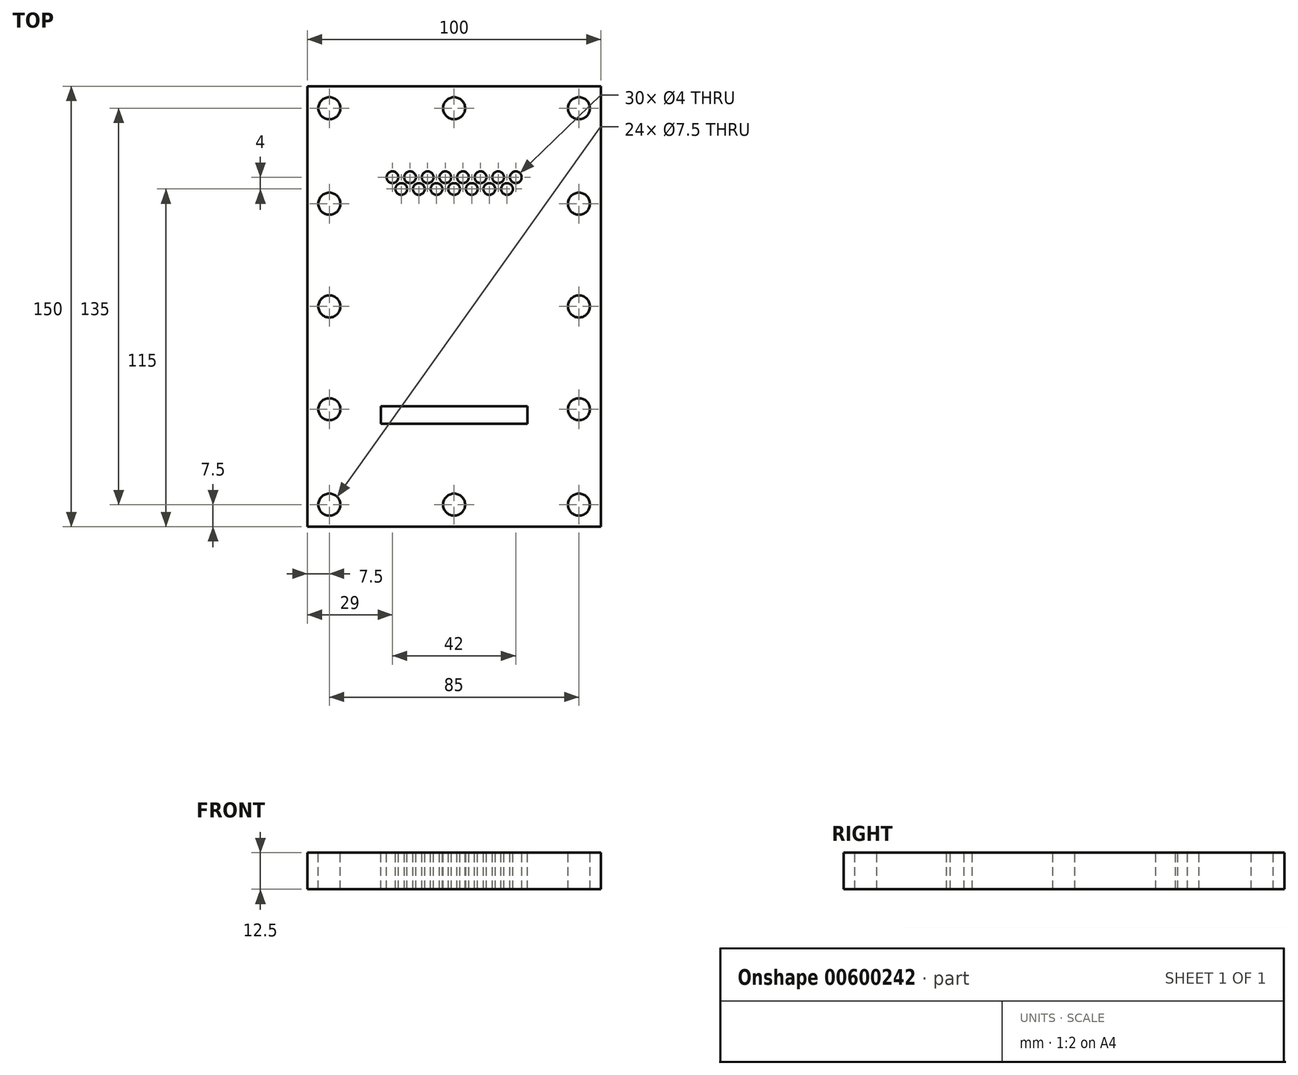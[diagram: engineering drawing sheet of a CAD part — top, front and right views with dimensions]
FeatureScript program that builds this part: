
annotation { "Feature Type Name" : "Feature", "Feature Type Description" : "" }
export const myFeature = defineFeature(function(context is Context, id is Id, definition is map)
    precondition{}
    {
        {
            var Q0;
            Q0=qCreatedBy(makeId("Top.planeOp"),FACE);
            var sketch = newSketch(context, id + "F0", { "sketchPlane" : qUnion([Q0])});
            skLineSegment(sketch, "E0.bottom", {"start": v(50, 75) * mm, "end": v(-50, 75) * mm});
            skLineSegment(sketch, "E0.top", {"start": v(50, -75) * mm, "end": v(-50, -75) * mm});
            skLineSegment(sketch, "E0.left", {"start": v(50, 75) * mm, "end": v(50, -75) * mm});
            skLineSegment(sketch, "E0.right", {"start": v(-50, 75) * mm, "end": v(-50, -75) * mm});
            skPoint(sketch, "E0.middle", {"position": v(0, 0) * mm});
            skSolve(sketch);
        }
        {
            var Q0;
            Q0=qSketchRegion(id+"F0",true);
            var Q1;
            Q1=qSketchRegion(id+"F2",true);
            extrude(context, id + "F1", {"entities" : qUnion([Q0, Q1]), "depth" : 12.5 * mm, "offsetDistance" : 25 * mm});
        }
        {
            var Q0;
            Q0=makeQuery(id+"F1.opExtrude","CAP_FACE",FACE,{"disambiguationData":[OSD([sQuery(id+"F0.wireOp",EDGE,"E0.bottom"),sQuery(id+"F0.wireOp",EDGE,"E0.top"),sQuery(id+"F0.wireOp",EDGE,"E0.left"),sQuery(id+"F0.wireOp",EDGE,"E0.right")])],"isStart":false});
            var sketch = newSketch(context, id + "F2", { "sketchPlane" : qUnion([Q0])});
            skCircle(sketch, "E1", {"center": v(-42.5, 67.5) * mm, "radius": 3.75 * mm});
            skCircle(sketch, "E2", {"center": v(-42.5, 0) * mm, "radius": 3.75 * mm});
            skCircle(sketch, "E3", {"center": v(-42.5, -35) * mm, "radius": 3.75 * mm});
            skCircle(sketch, "E4", {"center": v(-42.5, -67.5) * mm, "radius": 3.75 * mm});
            skCircle(sketch, "E5", {"center": v(0, -67.5) * mm, "radius": 3.75 * mm});
            skCircle(sketch, "E6", {"center": v(-42.5, 35) * mm, "radius": 3.75 * mm});
            skCircle(sketch, "E7", {"center": v(42.5, -67.5) * mm, "radius": 3.75 * mm});
            skCircle(sketch, "E8", {"center": v(42.5, -35) * mm, "radius": 3.75 * mm});
            skCircle(sketch, "E9", {"center": v(42.5, 0) * mm, "radius": 3.75 * mm});
            skCircle(sketch, "E10", {"center": v(42.5, 35) * mm, "radius": 3.75 * mm});
            skCircle(sketch, "E11", {"center": v(42.5, 67.5) * mm, "radius": 3.75 * mm});
            skCircle(sketch, "E12", {"center": v(0, 67.5) * mm, "radius": 3.75 * mm});
            skSolve(sketch);
        }
        {
            var Q0;
            Q0=qSketchRegion(id+"F2",true);
            extrude(context, id + "F3", {"entities" : qUnion([Q0]), "operationType" : NewBodyOperationType.REMOVE, "oppositeDirection" : true, "depth" : 25 * mm, "offsetDistance" : 25 * mm});
        }
        {
            var Q0;
            Q0=makeQuery(id+"F1.opExtrude","CAP_FACE",FACE,{"disambiguationData":[OSD([sQuery(id+"F0.wireOp",EDGE,"E0.bottom"),sQuery(id+"F0.wireOp",EDGE,"E0.top"),sQuery(id+"F0.wireOp",EDGE,"E0.left"),sQuery(id+"F0.wireOp",EDGE,"E0.right")])],"isStart":false});
            var sketch = newSketch(context, id + "F4", { "sketchPlane" : qUnion([Q0])});
            skLineSegment(sketch, "E13.bottom", {"start": v(25, -40) * mm, "end": v(-25, -40) * mm});
            skLineSegment(sketch, "E13.top", {"start": v(25, -34) * mm, "end": v(-25, -34) * mm});
            skLineSegment(sketch, "E13.left", {"start": v(25, -40) * mm, "end": v(25, -34) * mm});
            skLineSegment(sketch, "E13.right", {"start": v(-25, -40) * mm, "end": v(-25, -34) * mm});
            skPoint(sketch, "E13.middle", {"position": v(0, -37) * mm});
            skSolve(sketch);
        }
        {
            var Q0;
            Q0=qSketchRegion(id+"F4",true);
            extrude(context, id + "F5", {"entities" : qUnion([Q0]), "operationType" : NewBodyOperationType.REMOVE, "oppositeDirection" : true, "depth" : 25 * mm, "offsetDistance" : 25 * mm});
        }
        {
            var Q0;
            Q0=makeQuery(id+"F1.opExtrude","CAP_FACE",FACE,{"disambiguationData":[OSD([sQuery(id+"F0.wireOp",EDGE,"E0.bottom"),sQuery(id+"F0.wireOp",EDGE,"E0.top"),sQuery(id+"F0.wireOp",EDGE,"E0.left"),sQuery(id+"F0.wireOp",EDGE,"E0.right")])],"isStart":false});
            var sketch = newSketch(context, id + "F6", { "sketchPlane" : qUnion([Q0])});
            skCircle(sketch, "E14", {"center": v(-18, 40) * mm, "radius": 2 * mm});
            skCircle(sketch, "E15", {"center": v(-15, 44) * mm, "radius": 2 * mm});
            skCircle(sketch, "E16", {"center": v(-12, 40) * mm, "radius": 2 * mm});
            skCircle(sketch, "E17", {"center": v(-9, 44) * mm, "radius": 2 * mm});
            skCircle(sketch, "E18", {"center": v(-6, 40) * mm, "radius": 2 * mm});
            skCircle(sketch, "E19", {"center": v(0, 40) * mm, "radius": 2 * mm});
            skCircle(sketch, "E20", {"center": v(-3, 44) * mm, "radius": 2 * mm});
            skCircle(sketch, "E21", {"center": v(-21, 44) * mm, "radius": 2 * mm});
            skCircle(sketch, "E22", {"center": v(15, 44) * mm, "radius": 2 * mm});
            skCircle(sketch, "E23", {"center": v(6, 40) * mm, "radius": 2 * mm});
            skCircle(sketch, "E24", {"center": v(18, 40) * mm, "radius": 2 * mm});
            skCircle(sketch, "E25", {"center": v(3, 44) * mm, "radius": 2 * mm});
            skCircle(sketch, "E26", {"center": v(21, 44) * mm, "radius": 2 * mm});
            skCircle(sketch, "E27", {"center": v(12, 40) * mm, "radius": 2 * mm});
            skCircle(sketch, "E28", {"center": v(9, 44) * mm, "radius": 2 * mm});
            skSolve(sketch);
        }
        {
            var Q0;
            Q0 = qSketchRegion(id + "F6", true);
            extrude(context, id + "F7", {"entities" : qUnion([Q0]), "operationType" : NewBodyOperationType.REMOVE, "oppositeDirection" : true, "depth" : 25 * mm, "offsetDistance" : 25 * mm});
        }
    });
